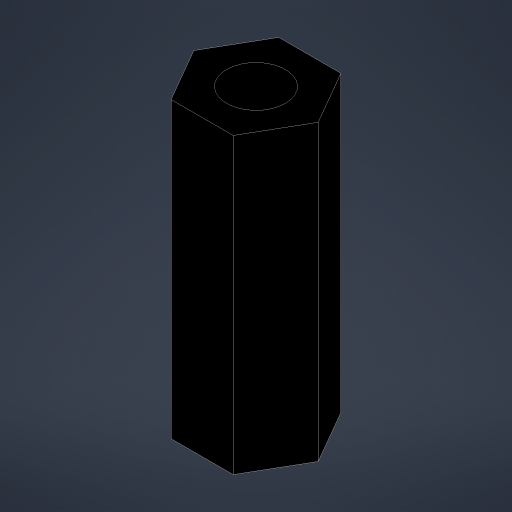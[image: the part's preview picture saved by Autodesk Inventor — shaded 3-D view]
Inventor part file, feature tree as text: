
AUTODESK INVENTOR PART (.ipt)
format: ipt  version: 2024.1 (Build 281209000, 209)  size: 159,744 bytes
history: native  units: mm
features: extrude x1, sketch x1
ambient origin geometry x8: Origin, YZ Plane, XZ Plane, XY Plane, X Axis, Y Axis, Z Axis, Center Point
bodies: Solid1 (feature_tree)
feature tree (2):
  extrude  "Extrusion1"  Depth=15.0mm
  sketch  "Sketch1"  dims[d0=5.5mm d1=3.0mm d2=15.0mm d3=0.0mm d4=0.5mm d5=0.872665mm]
